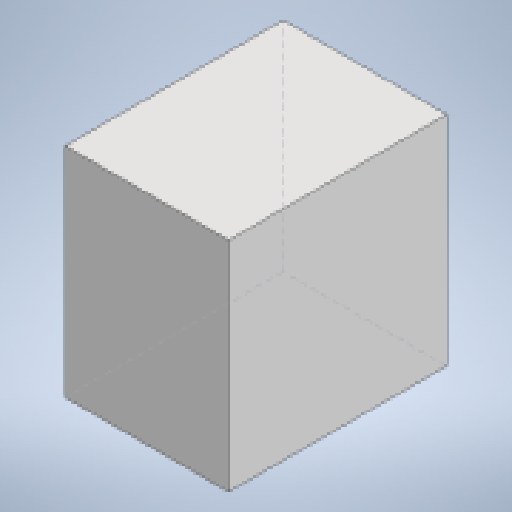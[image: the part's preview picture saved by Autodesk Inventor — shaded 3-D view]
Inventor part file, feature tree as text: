
AUTODESK INVENTOR PART (.ipt)
format: ipt  version: 2025 (Build 290162000, 162)  size: 192,000 bytes
history: native  units: mm
features: extrude x8, sketch x8, other x6, reference x1
ambient origin geometry x8: Origin, YZ Plane, XZ Plane, XY Plane, X Axis, Y Axis, Z Axis, Center Point
bodies: Body1 (feature_tree)
feature tree (23):
  other  "ソリッド1"
  extrude  "押し出し1"  Depth=30.0mm
  extrude  "押し出し2"  Depth=20.0mm
  extrude  "押し出し4"  Depth=15.0mm TaperAngle=0.0deg
  extrude  "押し出し5"  Depth=15.0mm
  extrude  "押し出し6"  Depth=10.0mm
  extrude  "押し出し7"  Depth=5.0mm
  extrude  "押し出し8"  Depth=5.0mm TaperAngle=0.0deg
  other  "ダイレクト編集1"
  extrude  "押し出し9"  TaperAngle=0.0deg  [1 undecoded]
  sketch  "スケッチ1"
  sketch  "スケッチ3"
  sketch  "スケッチ4"
  reference  "参照2"
  sketch  "スケッチ5"
  sketch  "スケッチ6"
  sketch  "スケッチ7"
  sketch  "スケッチ8"
  sketch  "スケッチ9"
  other  "<userpath>\Documents\設計データ\houseTools\trash-bag-hanger\design-data\trash-bag-hanger.iam"
  other  "trash-bag-hanger.iam"
  other  "arm-1:1"
  other  "移動1"
note: 1 required parameter value undecoded (feature->parameter linkage not recoverable at this tier; creation-order binding heuristic only, values carry confidence <= 0.55)
